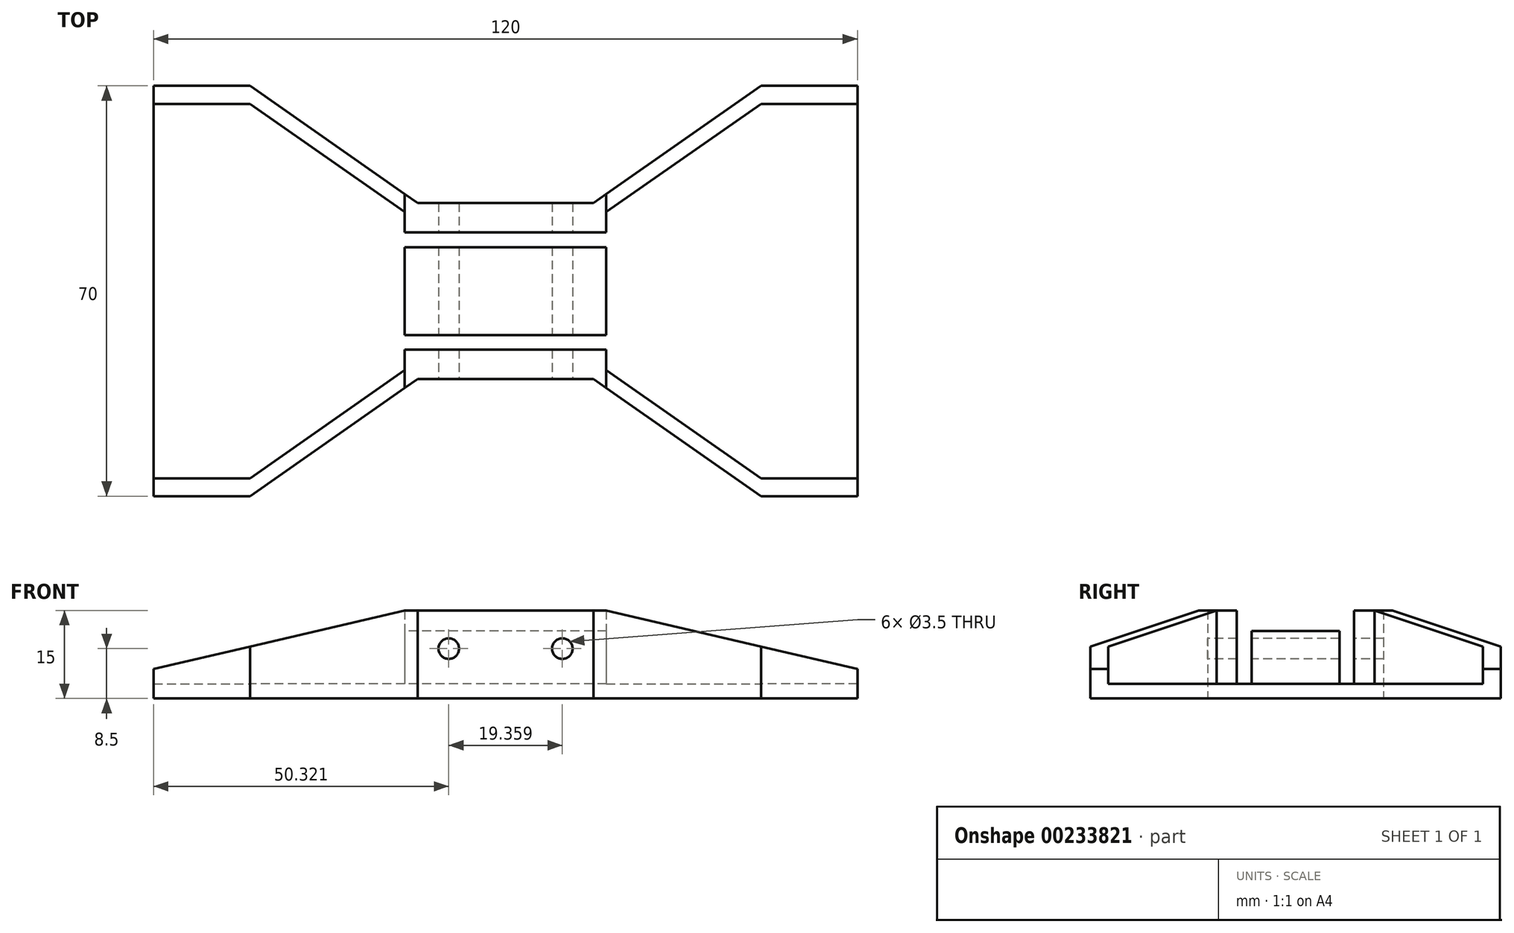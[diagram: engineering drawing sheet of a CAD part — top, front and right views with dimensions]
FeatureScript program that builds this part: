
annotation { "Feature Type Name" : "Feature", "Feature Type Description" : "" }
export const myFeature = defineFeature(function(context is Context, id is Id, definition is map)
    precondition{}
    {
        {
            var Q0;
            Q0=qCreatedBy(makeId("Top.planeOp"),FACE);
            var sketch = newSketch(context, id + "F0", { "sketchPlane" : qUnion([Q0])});
            skLineSegment(sketch, "E0.bottom", {"start": v(17.18, 7.5) * mm, "end": v(-17.18, 7.5) * mm});
            skLineSegment(sketch, "E0.top", {"start": v(17.18, -7.5) * mm, "end": v(-17.18, -7.5) * mm});
            skLineSegment(sketch, "E0.left", {"start": v(17.18, 7.5) * mm, "end": v(17.18, -7.5) * mm});
            skLineSegment(sketch, "E0.right", {"start": v(-17.18, 7.5) * mm, "end": v(-17.18, -7.5) * mm});
            skPoint(sketch, "E0.middle", {"position": v(0, 0) * mm});
            skLineSegment(sketch, "E1.bottom", {"start": v(-15, 15) * mm, "end": v(15, 15) * mm});
            skLineSegment(sketch, "E1.top", {"start": v(-17.18, 10) * mm, "end": v(17.18, 10) * mm});
            skLineSegment(sketch, "E1.left", {"start": v(-17.18, 13.47) * mm, "end": v(-17.18, 10) * mm});
            skLineSegment(sketch, "E1.right", {"start": v(17.18, 13.47) * mm, "end": v(17.18, 10) * mm});
            skLineSegment(sketch, "E2.bottom", {"start": v(-17.18, -10) * mm, "end": v(17.18, -10) * mm});
            skLineSegment(sketch, "E2.top", {"start": v(-15, -15) * mm, "end": v(15, -15) * mm});
            skLineSegment(sketch, "E2.left", {"start": v(-17.18, -10) * mm, "end": v(-17.18, -13.47) * mm});
            skLineSegment(sketch, "E2.right", {"start": v(17.18, -10) * mm, "end": v(17.18, -13.47) * mm});
            skLineSegment(sketch, "E3", {"start": v(-17.18, 13.47) * mm, "end": v(-43.56, 31.95) * mm});
            skLineSegment(sketch, "E4", {"start": v(-15, 15) * mm, "end": v(-43.56, 35) * mm});
            skLineSegment(sketch, "E5", {"start": v(-43.56, 35) * mm, "end": v(-60, 35) * mm});
            skLineSegment(sketch, "E6", {"start": v(-60, 35) * mm, "end": v(-60, 31.95) * mm});
            skLineSegment(sketch, "E7", {"start": v(-60, 31.95) * mm, "end": v(-43.56, 31.95) * mm});
            skLineSegment(sketch, "E8.MirrorCS", {"start": v(15, 15) * mm, "end": v(43.56, 35) * mm});
            skLineSegment(sketch, "E9.MirrorCS", {"start": v(17.18, 13.47) * mm, "end": v(43.56, 31.95) * mm});
            skLineSegment(sketch, "E10.MirrorCS", {"start": v(60, 31.95) * mm, "end": v(43.56, 31.95) * mm});
            skLineSegment(sketch, "E11.MirrorCS", {"start": v(43.56, 35) * mm, "end": v(60, 35) * mm});
            skLineSegment(sketch, "E12.MirrorCS", {"start": v(60, 35) * mm, "end": v(60, 31.95) * mm});
            skLineSegment(sketch, "E13", {"start": v(-17.18, 15) * mm, "end": v(-44.88, 34.4) * mm, "construction": true});
            skLineSegment(sketch, "E14.MirrorCS", {"start": v(-60, -35) * mm, "end": v(-60, -31.95) * mm});
            skLineSegment(sketch, "E15.MirrorCS", {"start": v(-60, -31.95) * mm, "end": v(-43.56, -31.95) * mm});
            skLineSegment(sketch, "E16.MirrorCS", {"start": v(-43.56, -35) * mm, "end": v(-60, -35) * mm});
            skLineSegment(sketch, "E17.MirrorCS", {"start": v(-17.18, -15) * mm, "end": v(-44.88, -34.4) * mm, "construction": true});
            skLineSegment(sketch, "E18.MirrorCS", {"start": v(-15, -15) * mm, "end": v(-43.56, -35) * mm});
            skLineSegment(sketch, "E19.MirrorCS", {"start": v(-17.18, -13.47) * mm, "end": v(-43.56, -31.95) * mm});
            skLineSegment(sketch, "E20.MirrorCS", {"start": v(60, -35) * mm, "end": v(60, -31.95) * mm});
            skLineSegment(sketch, "E21.MirrorCS", {"start": v(60, -31.95) * mm, "end": v(43.56, -31.95) * mm});
            skLineSegment(sketch, "E22.MirrorCS", {"start": v(43.56, -35) * mm, "end": v(60, -35) * mm});
            skLineSegment(sketch, "E23.MirrorCS", {"start": v(17.18, -13.47) * mm, "end": v(43.56, -31.95) * mm});
            skLineSegment(sketch, "E24.MirrorCS", {"start": v(15, -15) * mm, "end": v(43.56, -35) * mm});
            skLineSegment(sketch, "E25", {"start": v(-60, 31.95) * mm, "end": v(-60, -31.95) * mm});
            skLineSegment(sketch, "E26", {"start": v(60, 31.95) * mm, "end": v(60, -31.95) * mm});
            skPoint(sketch, "E27.orphan", {"position": v(17.18, -15) * mm});
            skSolve(sketch);
        }
        {
            var Q0;
            Q0=makeQuery(id+"F0.imprint","IMPRINT",FACE,{"disambiguationData":[TD([[makeQuery(id+"F0.imprint","IMPRINT",EDGE,{"derivedFrom":sQuery(id+"F0.wireOp",EDGE,"E0.bottom")}),1.0]])]});
            extrude(context, id + "F1", {"entities" : qUnion([Q0]), "depth" : 11.5 * mm});
        }
        {
            var Q0;
            Q0=makeQuery(id+"F0.imprint","IMPRINT",FACE,{"disambiguationData":[TD([[makeQuery(id+"F0.imprint","IMPRINT",EDGE,{"derivedFrom":sQuery(id+"F0.wireOp",EDGE,"E0.bottom")}),-1.0]])]});
            extrude(context, id + "F2", {"entities" : qUnion([Q0]), "operationType" : NewBodyOperationType.ADD, "depth" : 2.5 * mm});
        }
        {
            var Q0;
            Q0=makeQuery(id+"F0.imprint","IMPRINT",FACE,{"disambiguationData":[TD([[makeQuery(id+"F0.imprint","IMPRINT",EDGE,{"derivedFrom":sQuery(id+"F0.wireOp",EDGE,"E2.bottom")}),-1.0]])]});
            var Q1;
            Q1=makeQuery(id+"F0.imprint","IMPRINT",FACE,{"disambiguationData":[TD([[makeQuery(id+"F0.imprint","IMPRINT",EDGE,{"derivedFrom":sQuery(id+"F0.wireOp",EDGE,"E1.bottom")}),-1.0]])]});
            extrude(context, id + "F3", {"entities" : qUnion([Q0, Q1]), "operationType" : NewBodyOperationType.ADD, "depth" : 15 * mm});
        }
        {
            var Q0;
            Q0=makeQuery(id+"F3.opExtrude","SWEPT_FACE",FACE,{"disambiguationData":[OSD([sQuery(id+"F0.wireOp",EDGE,"E16.MirrorCS")])]});
            var sketch = newSketch(context, id + "F4", { "sketchPlane" : qUnion([Q0])});
            skPoint(sketch, "E28.0", {"position": v(60, 0) * mm});
            skPoint(sketch, "E29.0", {"position": v(60, 15) * mm});
            skPoint(sketch, "E30.0", {"position": v(-60, 15) * mm});
            skPoint(sketch, "E31.0", {"position": v(-60, 0) * mm});
            skLineSegment(sketch, "E32", {"start": v(-60, 0) * mm, "end": v(60, 0) * mm});
            skLineSegment(sketch, "E33", {"start": v(60, 15) * mm, "end": v(-60, 15) * mm});
            skLineSegment(sketch, "E34", {"start": v(-60, 0) * mm, "end": v(-60, 15) * mm});
            skLineSegment(sketch, "E35", {"start": v(60, 15) * mm, "end": v(60, 0) * mm});
            skLineSegment(sketch, "E36", {"start": v(-60, 5) * mm, "end": v(-17.18, 15) * mm});
            skPoint(sketch, "E37.0", {"position": v(-15, 15) * mm});
            skPoint(sketch, "E38.0", {"position": v(-17.18, 15) * mm});
            skLineSegment(sketch, "E39.MirrorCS", {"start": v(60, 5) * mm, "end": v(17.18, 15) * mm});
            skSolve(sketch);
        }
        {
            var Q0;
            {var subQ0=sQuery(id+"F4.wireOp",EDGE,"E34");var subQ1=sQuery(id+"F4.wireOp",EDGE,"E33");var subQ2=makeQuery(id+"F4.imprint","INTERSECT",VERTEX,{"derivedFrom":[subQ1,subQ0]});Q0=makeQuery(id+"F4.imprint","IMPRINT",FACE,{"disambiguationData":[TD([[makeQuery(id+"F4.imprint","IMPRINT",EDGE,{"disambiguationData":[TD([[subQ2,-1.0]])],"derivedFrom":subQ0}),1.0]])]});}
            var Q1;
            {var subQ0=sQuery(id+"F4.wireOp",EDGE,"E33");var subQ3=sQuery(id+"F4.wireOp",EDGE,"E36");var subQ4=makeQuery(id+"F4.imprint","INTERSECT",VERTEX,{"derivedFrom":[subQ0,subQ3]});Q1=makeQuery(id+"F4.imprint","IMPRINT",FACE,{"disambiguationData":[TD([[makeQuery(id+"F4.imprint","IMPRINT",EDGE,{"disambiguationData":[TD([[subQ4,-1.0]])],"derivedFrom":subQ0}),1.0]])]});}
            var Q2;
            {var subQ3=sQuery(id+"F4.wireOp",EDGE,"E39.MirrorCS");Q2=makeQuery(id+"F4.imprint","IMPRINT",FACE,{"disambiguationData":[TD([[makeQuery(id+"F4.imprint","IMPRINT",EDGE,{"derivedFrom":subQ3}),-1.0]])]});}
            var Q3;
            Q3=makeQuery(id+"F3.opExtrude","SWEPT_FACE",FACE,{"disambiguationData":[OSD([sQuery(id+"F0.wireOp",EDGE,"E11.MirrorCS")])]});
            extrude(context, id + "F5", {"entities" : qUnion([Q0, Q1, Q2]), "operationType" : NewBodyOperationType.REMOVE, "endBound" : BoundingType.UP_TO_SURFACE, "oppositeDirection" : true, "endBoundEntityFace" : qUnion([Q3]), "depth" : 25 * mm});
        }
        {
            var Q0;
            Q0=makeQuery(id+"F3.opExtrude","SWEPT_FACE",FACE,{"disambiguationData":[OSD([sQuery(id+"F0.wireOp",EDGE,"E2.top")])]});
            var sketch = newSketch(context, id + "F6", { "sketchPlane" : qUnion([Q0])});
            skCircle(sketch, "E40", {"center": v(-9.68, 8.5) * mm, "radius": 1.75 * mm});
            skCircle(sketch, "E41.MirrorC", {"center": v(9.68, 8.5) * mm, "radius": 1.75 * mm});
            skSolve(sketch);
        }
        {
            var Q0;
            Q0 = qSketchRegion(id + "F6", true);
            extrude(context, id + "F7", {"entities" : qUnion([Q0]), "operationType" : NewBodyOperationType.REMOVE, "endBound" : BoundingType.THROUGH_ALL, "oppositeDirection" : true, "depth" : 25 * mm});
        }
    });
